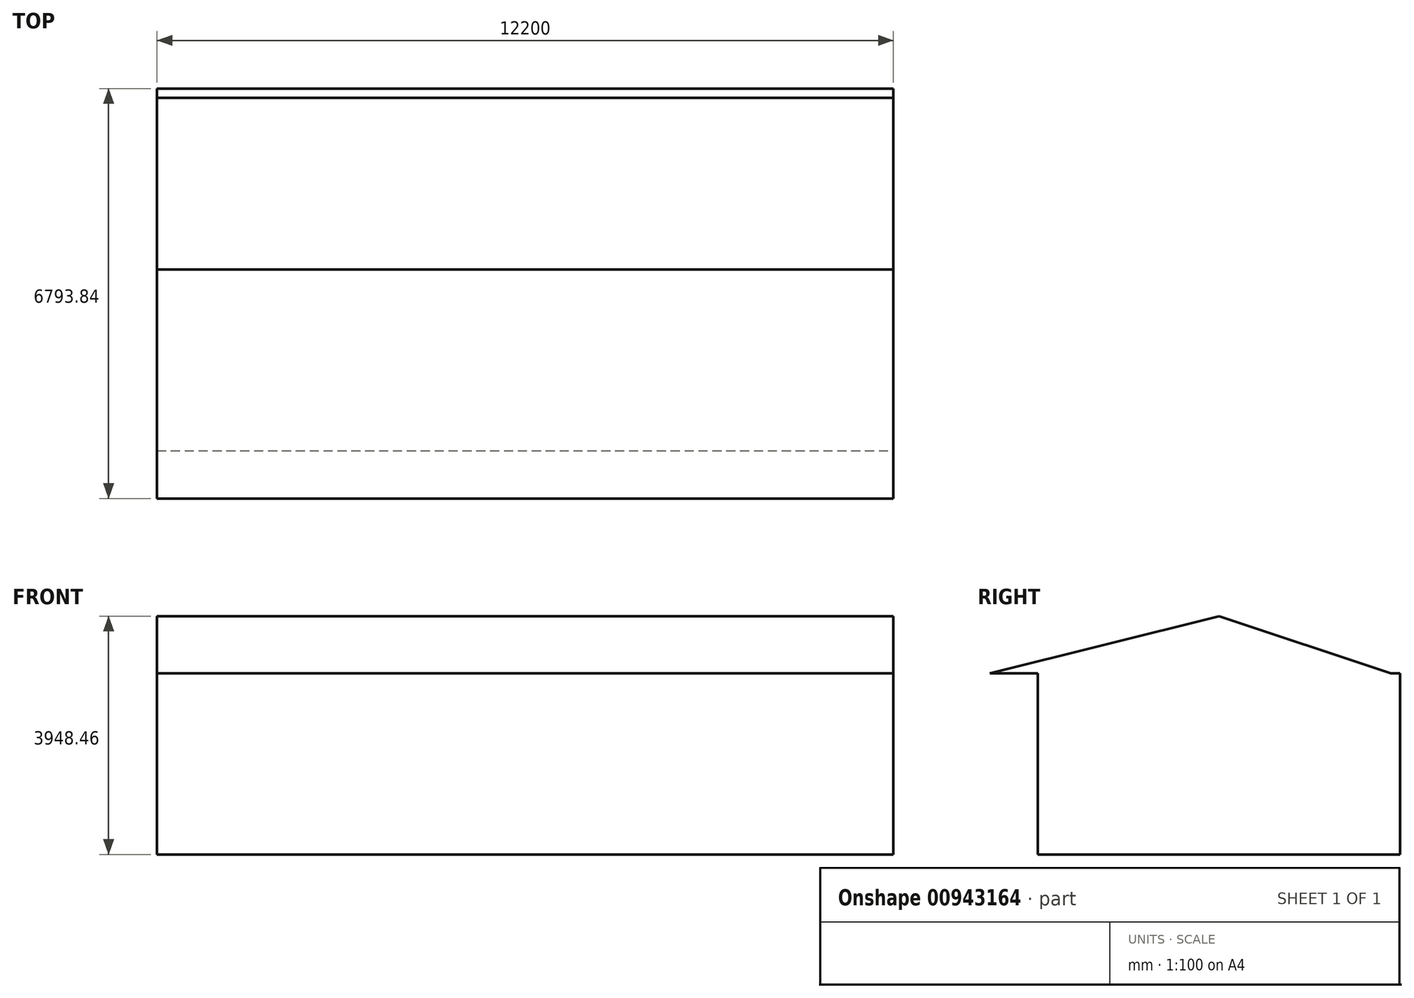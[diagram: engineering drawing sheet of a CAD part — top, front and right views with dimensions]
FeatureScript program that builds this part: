
annotation { "Feature Type Name" : "Feature", "Feature Type Description" : "" }
export const myFeature = defineFeature(function(context is Context, id is Id, definition is map)
    precondition{}
    {
        {
            var Q0;
            Q0=qCreatedBy(makeId("Top.planeOp"),FACE);
            var sketch = newSketch(context, id + "F0", { "sketchPlane" : qUnion([Q0])});
            skLineSegment(sketch, "E0.bottom", {"start": v(0, 0) * mm, "end": v(12200, 0) * mm});
            skLineSegment(sketch, "E0.top", {"start": v(0, -6000) * mm, "end": v(12200, -6000) * mm});
            skLineSegment(sketch, "E0.left", {"start": v(0, 0) * mm, "end": v(0, -6000) * mm});
            skLineSegment(sketch, "E0.right", {"start": v(12200, 0) * mm, "end": v(12200, -6000) * mm});
            skSolve(sketch);
        }
        {
            var Q0;
            Q0 = qSketchRegion(id + "F0", true);
            extrude(context, id + "F1", {"entities" : qUnion([Q0]), "depth" : 3000 * mm, "offsetDistance" : 25 * mm});
        }
        {
            var Q0;
            Q0=makeQuery(id+"F1.opExtrude","SWEPT_FACE",FACE,{"disambiguationData":[OSD([sQuery(id+"F0.wireOp",EDGE,"E0.left")])]});
            var sketch = newSketch(context, id + "F2", { "sketchPlane" : qUnion([Q0])});
            skLineSegment(sketch, "E1", {"start": v(0, 3000) * mm, "end": v(7000, 3000) * mm});
            skLineSegment(sketch, "E2", {"start": v(7000, 3000) * mm, "end": v(3000, 4000) * mm});
            skLineSegment(sketch, "E3", {"start": v(3000, 4000) * mm, "end": v(0, 3000) * mm});
            skSolve(sketch);
        }
        {
            var Q0;
            Q0 = qSketchRegion(id + "F2", true);
            extrude(context, id + "F3", {"entities" : qUnion([Q0]), "operationType" : NewBodyOperationType.ADD, "oppositeDirection" : true, "depth" : 12200 * mm, "offsetDistance" : 25 * mm});
        }
        {
            var Q0;
            Q0=makeQuery(id+"F3.boolean.opBoolean","MERGE",FACE,{"derivedFrom":[makeQuery(id+"F1.opExtrude","SWEPT_FACE",FACE,{"disambiguationData":[OSD([sQuery(id+"F0.wireOp",EDGE,"E0.left")])]}),makeQuery(id+"F3.opExtrude","CAP_FACE",FACE,{"disambiguationData":[OSD([sQuery(id+"F2.wireOp",EDGE,"E1"),sQuery(id+"F2.wireOp",EDGE,"E2"),sQuery(id+"F2.wireOp",EDGE,"E3")])],"isStart":true})]});
            var sketch = newSketch(context, id + "F4", { "sketchPlane" : qUnion([Q0])});
            skLineSegment(sketch, "E4", {"start": v(0, 3000) * mm, "end": v(3000, 4000) * mm});
            skLineSegment(sketch, "E5", {"start": v(3000, 4000) * mm, "end": v(7000, 3000) * mm});
            skLineSegment(sketch, "E6", {"start": v(7000, 3000) * mm, "end": v(6793.84, 3000) * mm});
            skLineSegment(sketch, "E7", {"start": v(6793.84, 3000) * mm, "end": v(3000, 3948.46) * mm});
            skLineSegment(sketch, "E8", {"start": v(3000, 3948.46) * mm, "end": v(154.62, 3000) * mm});
            skLineSegment(sketch, "E9", {"start": v(154.62, 3000) * mm, "end": v(0, 3000) * mm});
            skSolve(sketch);
        }
        {
            var Q0;
            Q0 = qSketchRegion(id + "F4", true);
            extrude(context, id + "F5", {"entities" : qUnion([Q0]), "operationType" : NewBodyOperationType.REMOVE, "oppositeDirection" : true, "depth" : 12200 * mm, "offsetDistance" : 25 * mm});
        }
    });
